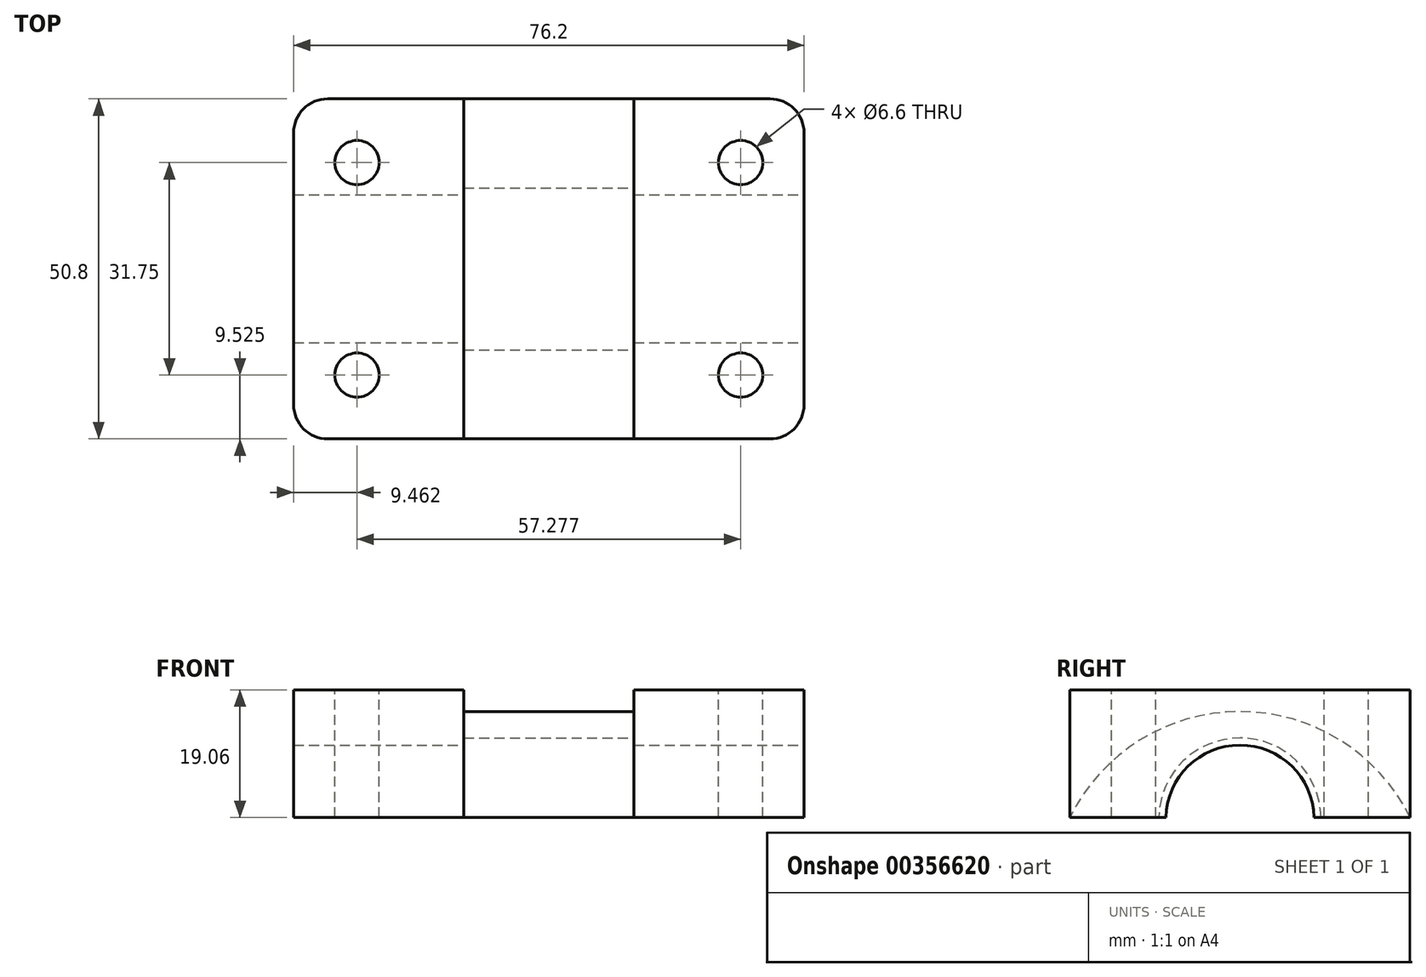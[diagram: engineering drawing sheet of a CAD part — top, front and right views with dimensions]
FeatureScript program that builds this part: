
annotation { "Feature Type Name" : "Feature", "Feature Type Description" : "" }
export const myFeature = defineFeature(function(context is Context, id is Id, definition is map)
    precondition{}
    {
        {
            var Q0;
            Q0=qCreatedBy(makeId("Front.planeOp"),FACE);
            var sketch = newSketch(context, id + "F0", { "sketchPlane" : qUnion([Q0])});
            skLineSegment(sketch, "E0.bottom", {"start": v(38.1, 9.53) * mm, "end": v(-38.1, 9.53) * mm});
            skLineSegment(sketch, "E0.top", {"start": v(38.1, -9.53) * mm, "end": v(-38.1, -9.53) * mm});
            skLineSegment(sketch, "E0.left", {"start": v(38.1, 9.53) * mm, "end": v(38.1, -9.52) * mm});
            skLineSegment(sketch, "E0.right", {"start": v(-38.1, 9.53) * mm, "end": v(-38.1, -9.53) * mm});
            skPoint(sketch, "E0.middle", {"position": v(0, 0) * mm});
            skSolve(sketch);
        }
        {
            var Q0;
            Q0=makeQuery(id+"F0.imprint","IMPRINT",FACE,{"disambiguationData":[TD([[makeQuery(id+"F0.imprint","IMPRINT",EDGE,{"derivedFrom":sQuery(id+"F0.wireOp",EDGE,"E0.bottom")}),1.0]])]});
            var Q1;
            Q1 = qSketchRegion(id + "F2", true);
            extrude(context, id + "F1", {"entities" : qUnion([Q0, Q1]), "depth" : 50.8 * mm, "symmetric" : true});
        }
        {
            var Q0;
            Q0=makeQuery(id+"F1.opExtrude","SWEPT_FACE",FACE,{"disambiguationData":[OSD([sQuery(id+"F0.wireOp",EDGE,"E0.left")])]});
            var sketch = newSketch(context, id + "F2", { "sketchPlane" : qUnion([Q0])});
            skLineSegment(sketch, "E1.bottom", {"start": v(11.05, -9.52) * mm, "end": v(-11.05, -9.52) * mm});
            skPoint(sketch, "E1.middle", {"position": v(0, 0) * mm});
            skArc(sketch, "E2", {"start": v(11.05, -9.52) * mm, "mid": v(0, 1.27) * mm, "end": v(-11.05, -9.52) * mm});
            skLineSegment(sketch, "E3", {"start": v(-11.05, -9.52) * mm, "end": v(-12.13, -9.52) * mm});
            skLineSegment(sketch, "E4", {"start": v(11.05, -9.52) * mm, "end": v(12.1, -9.52) * mm});
            skLineSegment(sketch, "E5", {"start": v(0, 1.27) * mm, "end": v(0, 2.34) * mm});
            skArc(sketch, "E6", {"start": v(12.1, -9.52) * mm, "mid": v(-0.01, 2.34) * mm, "end": v(-12.13, -9.52) * mm});
            skArc(sketch, "E7", {"start": v(25.4, -9.52) * mm, "mid": v(0, 6.27) * mm, "end": v(-25.4, -9.52) * mm});
            skSolve(sketch);
        }
        {
            var Q0;
            {var subQ0=sQuery(id+"F2.wireOp",EDGE,"E1.bottom");Q0=makeQuery(id+"F2.imprint","IMPRINT",FACE,{"disambiguationData":[TD([[makeQuery(id+"F2.imprint","IMPRINT",EDGE,{"derivedFrom":subQ0}),1.0]])]});}
            extrude(context, id + "F3", {"entities" : qUnion([Q0]), "operationType" : NewBodyOperationType.REMOVE, "oppositeDirection" : true, "depth" : 76.2 * mm});
        }
        {
            var Q0;
            {var subQ0=sQuery(id+"F2.wireOp",EDGE,"E3");Q0=makeQuery(id+"F2.imprint","IMPRINT",FACE,{"disambiguationData":[TD([[makeQuery(id+"F2.imprint","IMPRINT",EDGE,{"derivedFrom":subQ0}),1.0]])]});}
            var Q1;
            {var subQ0=sQuery(id+"F2.wireOp",EDGE,"E4");Q1=makeQuery(id+"F2.imprint","IMPRINT",FACE,{"disambiguationData":[TD([[makeQuery(id+"F2.imprint","IMPRINT",EDGE,{"derivedFrom":subQ0}),1.0]])]});}
            var Q2;
            {var subQ0=sQuery(id+"F2.wireOp",EDGE,"E1.bottom");Q2=makeQuery(id+"F2.imprint","IMPRINT",FACE,{"disambiguationData":[TD([[makeQuery(id+"F2.imprint","IMPRINT",EDGE,{"derivedFrom":subQ0}),1.0]])]});}
            extrude(context, id + "F4", {"entities" : qUnion([Q0, Q1, Q2]), "operationType" : NewBodyOperationType.REMOVE, "oppositeDirection" : true, "depth" : 50.8 * mm, "hasSecondDirection" : true, "secondDirectionOppositeDirection" : true, "secondDirectionDepth" : 25.4 * mm});
        }
        {
            var Q0;
            {var subQ0=sQuery(id+"F0.wireOp",EDGE,"E0.right");var subQ1=sQuery(id+"F0.wireOp",EDGE,"E0.left");var subQ2=sQuery(id+"F0.wireOp",EDGE,"E0.top");Q0=makeQuery(id+"F3.boolean.opBoolean","SPLIT",FACE,{"disambiguationData":[TD([makeQuery(id+"F1.opExtrude","CAP_FACE",FACE,{"disambiguationData":[OSD([sQuery(id+"F0.wireOp",EDGE,"E0.bottom"),subQ2,subQ1,subQ0])],"isStart":false})])],"derivedFrom":makeQuery(id+"F1.opExtrude","SWEPT_FACE",FACE,{"disambiguationData":[OSD([subQ2])]})});}
            var sketch = newSketch(context, id + "F5", { "sketchPlane" : qUnion([Q0])});
            skLineSegment(sketch, "E8.bottom", {"start": v(-28.64, 15.88) * mm, "end": v(28.64, 15.88) * mm});
            skLineSegment(sketch, "E8.top", {"start": v(-28.64, -15.88) * mm, "end": v(28.64, -15.88) * mm});
            skLineSegment(sketch, "E8.left", {"start": v(-28.64, 15.88) * mm, "end": v(-28.64, -15.88) * mm});
            skLineSegment(sketch, "E8.right", {"start": v(28.64, 15.88) * mm, "end": v(28.64, -15.88) * mm});
            skPoint(sketch, "E8.middle", {"position": v(0, 0) * mm});
            skSolve(sketch);
        }
        {
            var Q0;
            Q0=sQuery(id+"F5.wireOp",VERTEX,"E8.left.start");
            var Q1;
            Q1=sQuery(id+"F5.wireOp",VERTEX,"E8.right.start");
            var Q2;
            Q2=sQuery(id+"F5.wireOp",VERTEX,"E8.right.end");
            var Q3;
            Q3=sQuery(id+"F5.wireOp",VERTEX,"E8.left.end");
            var Q4;
            Q4=makeQuery(id+"F1.opExtrude","SWEPT_BODY",BODY,{"disambiguationData":[OSD([sQuery(id+"F0.wireOp",EDGE,"E0.bottom"),sQuery(id+"F0.wireOp",EDGE,"E0.top"),sQuery(id+"F0.wireOp",EDGE,"E0.left"),sQuery(id+"F0.wireOp",EDGE,"E0.right")])]});
            hole(context, id + "F6", {"style" : HoleStyle.SIMPLE, "endStyle" : HoleEndStyle.THROUGH, "holeDiameter" : 6.6 * mm, "isTappedThrough" : true, "tappedDepth" : 12.7 * mm, "tapClearance" : 3, "locations" : qUnion([Q0, Q1, Q2, Q3]), "scope" : qUnion([Q4])});
        }
        {
            var Q0;
            Q0 = qSketchRegion(id + "F2", true);
            var Q1;
            Q1=makeQuery(id+"F2.imprint","IMPRINT",FACE,{"disambiguationData":[TD([[makeQuery(id+"F2.imprint","IMPRINT",EDGE,{"derivedFrom":sQuery(id+"F2.wireOp",EDGE,"E7")}),-1.0]])]});
            extrude(context, id + "F7", {"entities" : qUnion([Q0, Q1]), "operationType" : NewBodyOperationType.REMOVE, "oppositeDirection" : true, "depth" : 50.8 * mm, "hasSecondDirection" : true, "secondDirectionOppositeDirection" : true, "secondDirectionDepth" : 25.4 * mm});
        }
        {
            var Q0;
            Q0=makeQuery(id+"F7.boolean.opBoolean","COPY",EDGE,{"derivedFrom":makeQuery(id+"F7.opExtrude","CAP_EDGE",EDGE,{"disambiguationData":[OSD([sQuery(id+"F0.wireOp",EDGE,"E0.bottom"),sQuery(id+"F0.wireOp",EDGE,"E0.left")])],"isStart":true})});
            var Q1;
            Q1=makeQuery(id+"F7.boolean.opBoolean","COPY",EDGE,{"derivedFrom":makeQuery(id+"F7.opExtrude","CAP_EDGE",EDGE,{"disambiguationData":[OSD([sQuery(id+"F0.wireOp",EDGE,"E0.bottom"),sQuery(id+"F0.wireOp",EDGE,"E0.left")])],"isStart":false})});
            var Q2;
            {var subQ0=sQuery(id+"F0.wireOp",EDGE,"E0.left");Q2=makeQuery(id+"F7.boolean.opBoolean","COPY",EDGE,{"derivedFrom":makeQuery(id+"F7.opExtrude","CAP_EDGE",EDGE,{"disambiguationData":[OSD([subQ0]),TDD([makeQuery(id+"F2.imprint","IMPRINT",EDGE,{"derivedFrom":makeQuery(id+"F1.opExtrude","CAP_EDGE",EDGE,{"disambiguationData":[OSD([subQ0])],"isStart":true})})])],"isStart":false})});}
            var Q3;
            {var subQ0=sQuery(id+"F0.wireOp",EDGE,"E0.left");Q3=makeQuery(id+"F7.boolean.opBoolean","COPY",EDGE,{"derivedFrom":makeQuery(id+"F7.opExtrude","CAP_EDGE",EDGE,{"disambiguationData":[OSD([subQ0]),TDD([makeQuery(id+"F2.imprint","IMPRINT",EDGE,{"derivedFrom":makeQuery(id+"F1.opExtrude","CAP_EDGE",EDGE,{"disambiguationData":[OSD([subQ0])],"isStart":true})})])],"isStart":true})});}
            var Q4;
            {var subQ0=sQuery(id+"F0.wireOp",EDGE,"E0.left");Q4=makeQuery(id+"F7.boolean.opBoolean","COPY",EDGE,{"derivedFrom":makeQuery(id+"F7.opExtrude","CAP_EDGE",EDGE,{"disambiguationData":[OSD([subQ0]),TDD([makeQuery(id+"F2.imprint","IMPRINT",EDGE,{"derivedFrom":makeQuery(id+"F1.opExtrude","CAP_EDGE",EDGE,{"disambiguationData":[OSD([subQ0])],"isStart":false})})])],"isStart":true})});}
            var Q5;
            {var subQ0=sQuery(id+"F0.wireOp",EDGE,"E0.left");Q5=makeQuery(id+"F7.boolean.opBoolean","COPY",EDGE,{"derivedFrom":makeQuery(id+"F7.opExtrude","CAP_EDGE",EDGE,{"disambiguationData":[OSD([subQ0]),TDD([makeQuery(id+"F2.imprint","IMPRINT",EDGE,{"derivedFrom":makeQuery(id+"F1.opExtrude","CAP_EDGE",EDGE,{"disambiguationData":[OSD([subQ0])],"isStart":false})})])],"isStart":false})});}
            var Q6;
            Q6=makeQuery(id+"F1.opExtrude","CAP_EDGE",EDGE,{"disambiguationData":[OSD([sQuery(id+"F0.wireOp",EDGE,"E0.right")])],"isStart":false});
            var Q7;
            Q7=makeQuery(id+"F1.opExtrude","CAP_EDGE",EDGE,{"disambiguationData":[OSD([sQuery(id+"F0.wireOp",EDGE,"E0.right")])],"isStart":true});
            var Q8;
            Q8=makeQuery(id+"F1.opExtrude","CAP_EDGE",EDGE,{"disambiguationData":[OSD([sQuery(id+"F0.wireOp",EDGE,"E0.left")])],"isStart":false});
            var Q9;
            Q9=makeQuery(id+"F1.opExtrude","CAP_EDGE",EDGE,{"disambiguationData":[OSD([sQuery(id+"F0.wireOp",EDGE,"E0.left")])],"isStart":true});
            fillet(context, id + "F8", {"entities" : qUnion([Q0, Q1, Q2, Q3, Q4, Q5, Q6, Q7, Q8, Q9]), "radius" : 5.08 * mm, "tangentPropagation" : true, "allowEdgeOverflow" : false});
        }
    });
